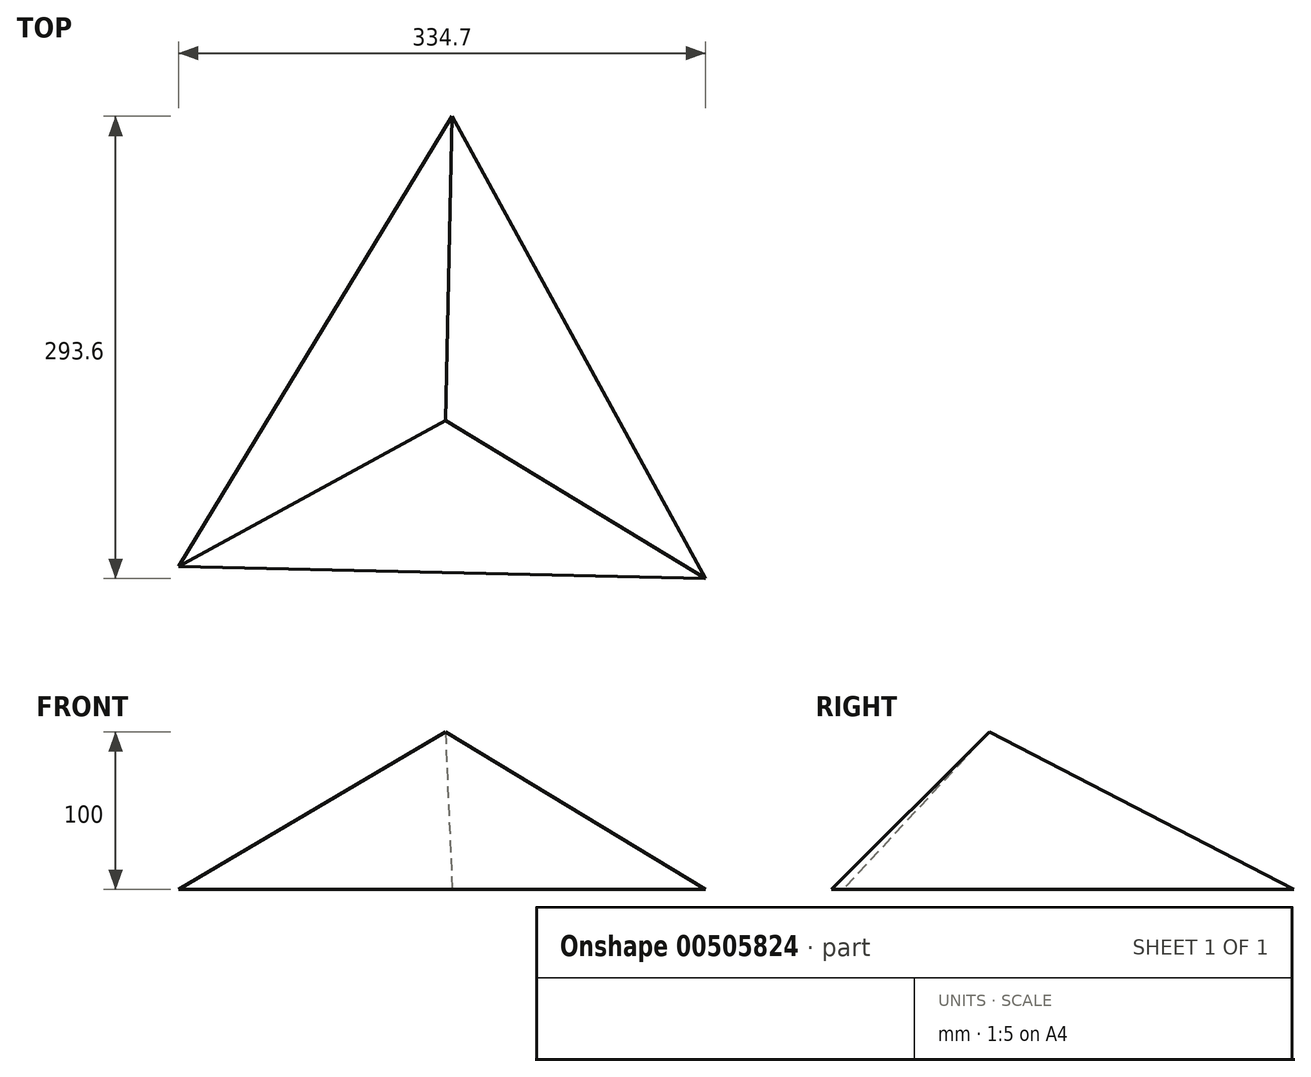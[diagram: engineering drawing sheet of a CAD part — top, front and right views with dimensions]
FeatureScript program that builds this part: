
annotation { "Feature Type Name" : "Feature", "Feature Type Description" : "" }
export const myFeature = defineFeature(function(context is Context, id is Id, definition is map)
    precondition{}
    {
        {
            var Q0;
            Q0=qCreatedBy(makeId("Top.planeOp"),FACE);
            var sketch = newSketch(context, id + "F0", { "sketchPlane" : qUnion([Q0])});
            skCircle(sketch, "E0.cCircle", {"center": v(0, 0) * mm, "radius": 96.65 * mm, "construction": true});
            skLineSegment(sketch, "E0.0", {"start": v(-169.51, -92.88) * mm, "end": v(4.32, 193.24) * mm});
            skLineSegment(sketch, "E0.1", {"start": v(4.32, 193.24) * mm, "end": v(165.2, -100.36) * mm});
            skLineSegment(sketch, "E0.2", {"start": v(165.2, -100.36) * mm, "end": v(-169.51, -92.88) * mm});
            skPoint(sketch, "E0.0.midPoint", {"position": v(-82.6, 50.18) * mm});
            skSolve(sketch);
        }
        {
            var Q0;
            Q0=qCreatedBy(makeId("Top.planeOp"),FACE);
            cPlane(context, id + "F1", {"entities" : qUnion([Q0]), "cplaneType" : CPlaneType.OFFSET, "offset" : 100 * mm, "width" : 150 * mm, "height" : 150 * mm});
        }
        {
            var Q0;
            Q0=qCreatedBy(id+"F1.planeOp",FACE);
            var sketch = newSketch(context, id + "F2", { "sketchPlane" : qUnion([Q0])});
            skPoint(sketch, "E1", {"position": v(0, 0) * mm});
            skSolve(sketch);
        }
        {
            var Q0;
            Q0=sQuery(id+"F2.wireOp",VERTEX,"E1");
            var Q1;
            Q1=makeQuery(id+"F0.imprint","IMPRINT",FACE,{"disambiguationData":[TD([[makeQuery(id+"F0.imprint","IMPRINT",EDGE,{"derivedFrom":sQuery(id+"F0.wireOp",EDGE,"E0.0")}),-1.0]])]});
            loft(context, id + "F3", {"sheetProfilesArray" : [{ "sheetProfileEntities" : qUnion([Q0]) }, { "sheetProfileEntities" : qUnion([Q1]) }]});
        }
    });
